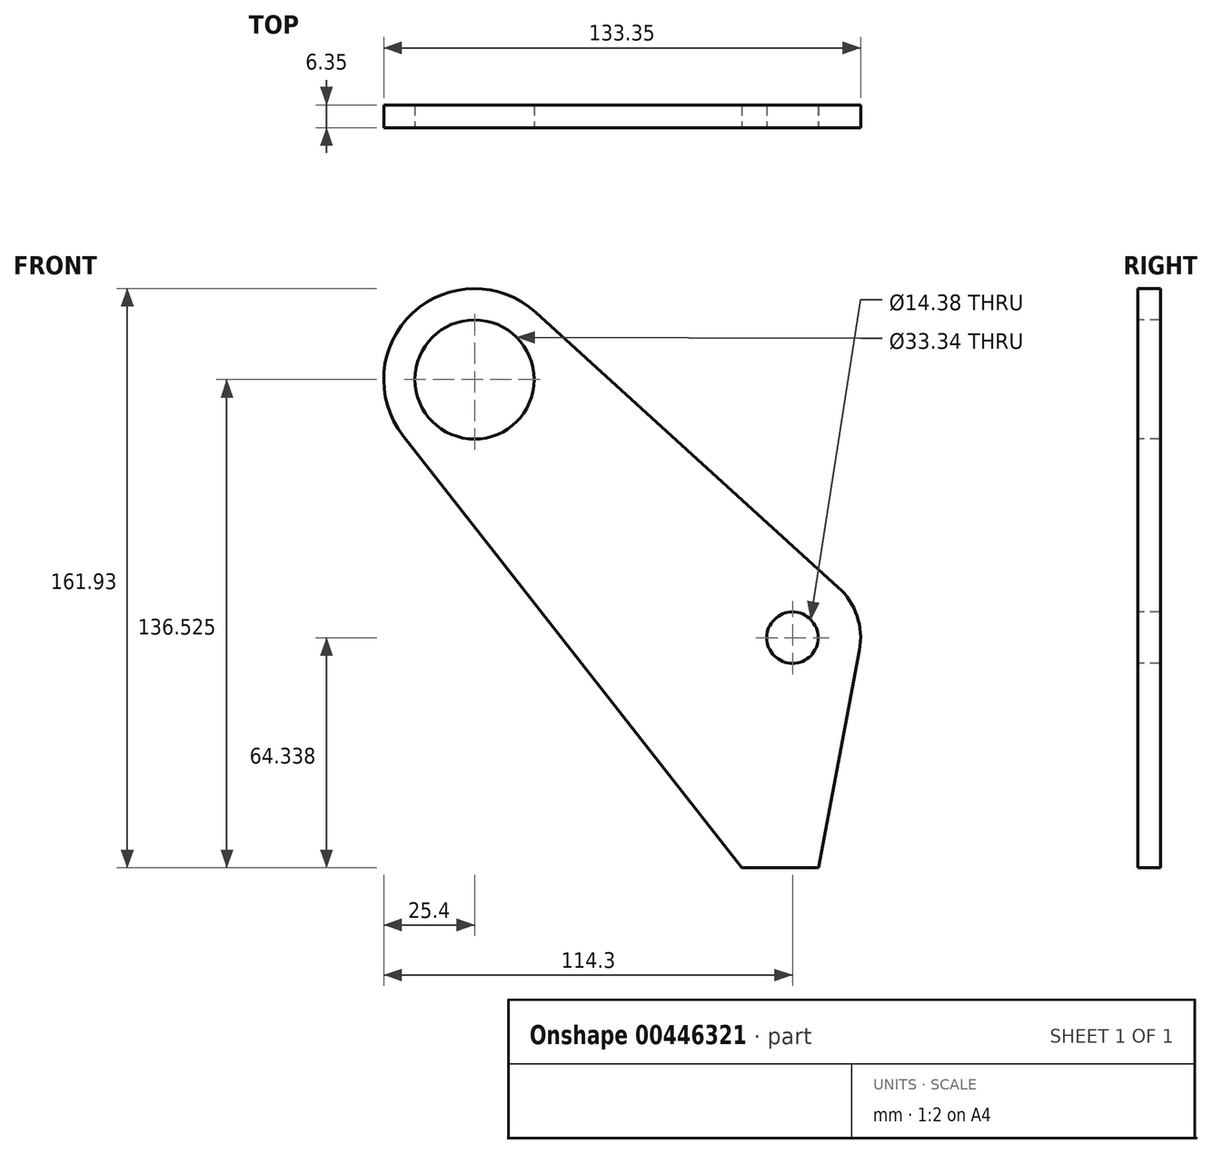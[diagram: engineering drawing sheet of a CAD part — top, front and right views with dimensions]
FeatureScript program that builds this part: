
annotation { "Feature Type Name" : "Feature", "Feature Type Description" : "" }
export const myFeature = defineFeature(function(context is Context, id is Id, definition is map)
    precondition{}
    {
        {
            var Q0;
            Q0=qCreatedBy(makeId("Front.planeOp"),FACE);
            var sketch = newSketch(context, id + "F0", { "sketchPlane" : qUnion([Q0])});
            skLineSegment(sketch, "E0", {"start": v(-454.06, 0) * mm, "end": v(343.4, 0) * mm, "construction": true});
            skPoint(sketch, "E1", {"position": v(0, 136.53) * mm});
            skCircle(sketch, "E2", {"center": v(0, 136.53) * mm, "radius": 16.67 * mm});
            skLineSegment(sketch, "E3", {"start": v(-51.75, 161.92) * mm, "end": v(165.67, 161.93) * mm, "construction": true});
            skLineSegment(sketch, "E4", {"start": v(25.4, 6.35) * mm, "end": v(82.55, 6.35) * mm});
            skLineSegment(sketch, "E5", {"start": v(25.4, 57.15) * mm, "end": v(212.05, 57.15) * mm});
            skCircle(sketch, "E6", {"center": v(88.9, 64.34) * mm, "radius": 7.19 * mm});
            skCircle(sketch, "E7", {"center": v(0, 136.53) * mm, "radius": 136.53 * mm, "construction": true});
            skLineSegment(sketch, "E8", {"start": v(25.4, 57.15) * mm, "end": v(25.4, 6.35) * mm});
            skPoint(sketch, "E9", {"position": v(121.83, 198.14) * mm});
            skLineSegment(sketch, "E10.bottom", {"start": v(134.14, 161.93) * mm, "end": v(184.88, 161.93) * mm});
            skLineSegment(sketch, "E10.top", {"start": v(134.14, 224.58) * mm, "end": v(184.88, 224.58) * mm});
            skLineSegment(sketch, "E10.left", {"start": v(134.14, 161.93) * mm, "end": v(134.14, 224.58) * mm});
            skLineSegment(sketch, "E10.right", {"start": v(184.88, 161.93) * mm, "end": v(184.88, 224.58) * mm});
            skLineSegment(sketch, "E11", {"start": v(134.14, 187.33) * mm, "end": v(184.88, 187.33) * mm});
            skLineSegment(sketch, "E12", {"start": v(82.55, 6.35) * mm, "end": v(96.17, 0) * mm});
            skLineSegment(sketch, "E13", {"start": v(25.4, 6.35) * mm, "end": v(25.4, 0) * mm});
            skLineSegment(sketch, "E14", {"start": v(25.4, 0) * mm, "end": v(96.17, 0) * mm});
            skLineSegment(sketch, "E15", {"start": v(17.08, 155.32) * mm, "end": v(101.7, 78.44) * mm});
            skArc(sketch, "E16", {"start": v(17.08, 155.32) * mm, "mid": v(-17.3, 155.13) * mm, "end": v(-20, 120.86) * mm});
            skArc(sketch, "E17", {"start": v(107.62, 60.81) * mm, "mid": v(106.96, 70.4) * mm, "end": v(101.7, 78.44) * mm});
            skLineSegment(sketch, "E18", {"start": v(96.17, 0) * mm, "end": v(107.62, 60.81) * mm});
            skLineSegment(sketch, "E19", {"start": v(-20, 120.86) * mm, "end": v(74.73, 0) * mm});
            skLineSegment(sketch, "E20", {"start": v(-65.22, 127.15) * mm, "end": v(109.95, -32) * mm, "construction": true});
            skPoint(sketch, "E21", {"position": v(82.55, 3.18) * mm});
            skPoint(sketch, "E22", {"position": v(77.12, 19.05) * mm});
            skLineSegment(sketch, "E23", {"start": v(0, 136.53) * mm, "end": v(0, 103.25) * mm});
            skLineSegment(sketch, "E24", {"start": v(0, 103.25) * mm, "end": v(38.1, 19.05) * mm});
            skPoint(sketch, "E25", {"position": v(28.57, 3.17) * mm});
            skSolve(sketch);
        }
        {
            var Q0;
            Q0=makeQuery(id+"F0.imprint","IMPRINT",FACE,{"disambiguationData":[TD([[makeQuery(id+"F0.imprint","IMPRINT",EDGE,{"derivedFrom":sQuery(id+"F0.wireOp",EDGE,"E2")}),-1.0]])]});
            var Q1;
            {var subQ0=sQuery(id+"F0.wireOp",EDGE,"E12");Q1=makeQuery(id+"F0.imprint","IMPRINT",FACE,{"disambiguationData":[TD([[makeQuery(id+"F0.imprint","IMPRINT",EDGE,{"derivedFrom":subQ0}),1.0]])]});}
            var Q2;
            {var subQ0=sQuery(id+"F0.wireOp",EDGE,"E12");Q2=makeQuery(id+"F0.imprint","IMPRINT",FACE,{"disambiguationData":[TD([[makeQuery(id+"F0.imprint","IMPRINT",EDGE,{"derivedFrom":subQ0}),-1.0]])]});}
            extrude(context, id + "F1", {"entities" : qUnion([Q0, Q1, Q2]), "oppositeDirection" : true, "depth" : 6.35 * mm, "offsetDistance" : 25.4 * mm});
        }
    });
